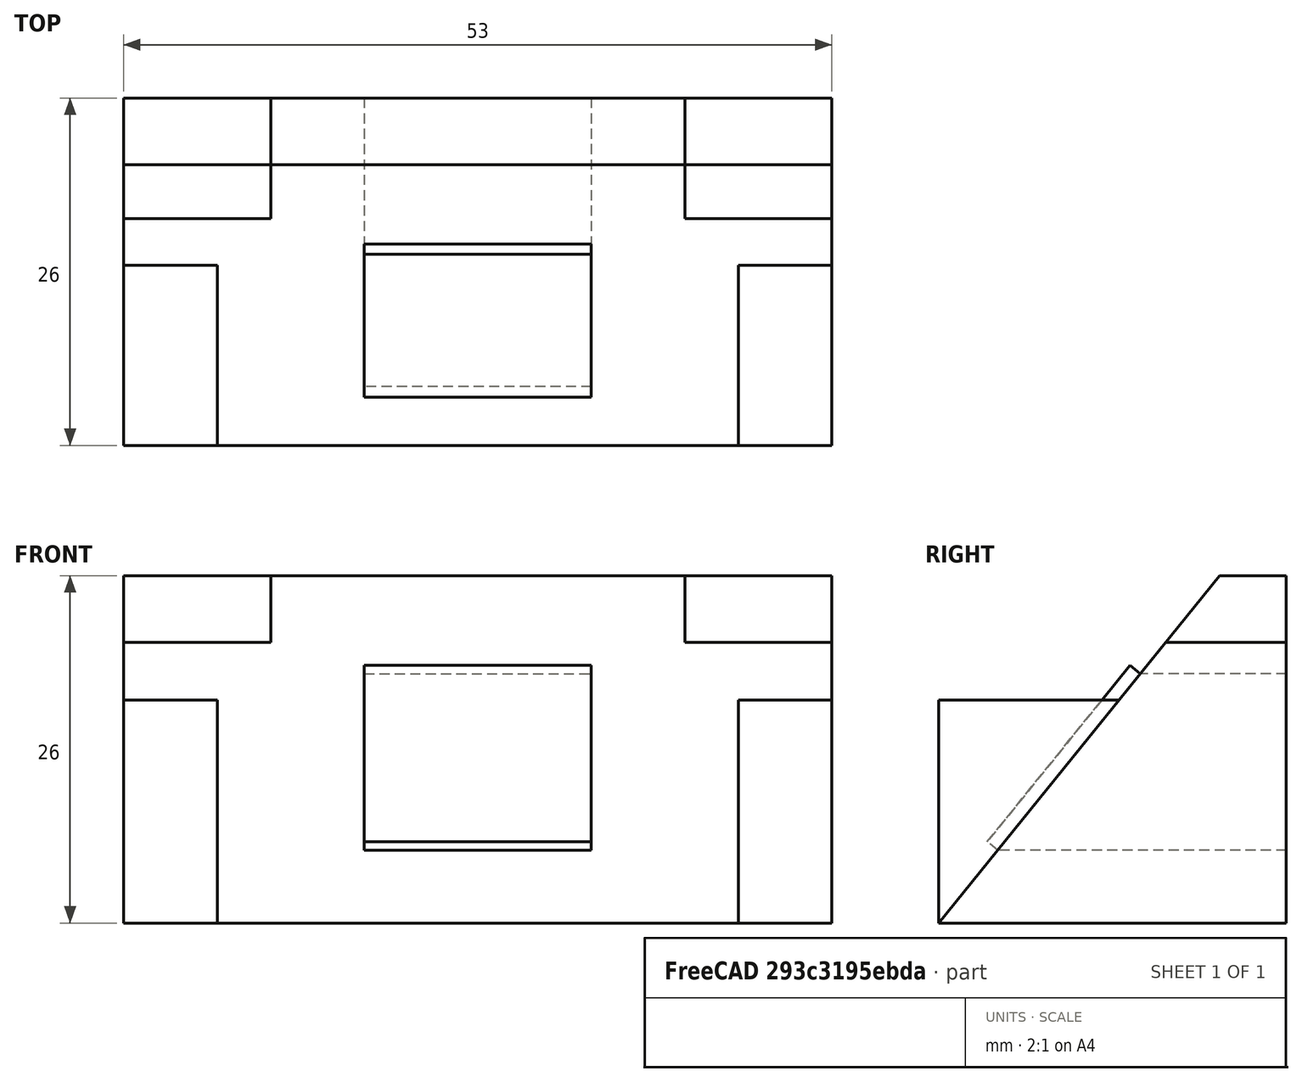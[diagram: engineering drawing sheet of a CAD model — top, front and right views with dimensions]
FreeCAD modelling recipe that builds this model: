
FCSTD DOCUMENT  (FreeCAD 0.16R)
Label: tutorial1
License: All rights reserved
LicenseURL: http://en.wikipedia.org/wiki/All_rights_reserved
objects: Sketcher::SketchObject×5, PartDesign::Pad×3, PartDesign::Pocket×2, PartDesign::Mirrored×2, Mesh::Feature×2, Part::FeaturePython×1
note: 18 computed .brp shape members not serialized (recipe doc carries the construction recipe); baked Part::Feature solids carry a one-line shape summary decoded from their .brp

FEATURE [Sketcher::SketchObject] Sketch
  Placement = pos=(0,0,0) rot=(0.57735,0.57735,0.57735;2.0944rad)
  sketch-geometry (4):
    g0: LineSegment StartX=8 StartY=13 StartZ=0 EndX=13 EndY=13 EndZ=0
    g1: LineSegment StartX=13 StartY=13 StartZ=0 EndX=13 EndY=-13 EndZ=0
    g2: LineSegment StartX=13 StartY=-13 StartZ=0 EndX=-13 EndY=-13 EndZ=0
    g3: LineSegment StartX=-13 StartY=-13 StartZ=0 EndX=8 EndY=13 EndZ=0
  constraints (11):
    c: Coincident(g0,g1)
    c: Vertical(g1)
    c: Coincident(g1,g2)
    c: Horizontal(g2)
    c: Coincident(g2,g3)
    c: Horizontal(g0)
    c: Coincident(g3,g0)
    c: DistanceX(g2,g2) = 26
    c: DistanceX(g0,g0) = 5
    c: Equal(g2,g1)
    c: Symmetric(g2,g0,g-1)
FEATURE [PartDesign::Pad] Pad
  Length = 53
  Length2 = 1
  Midplane = true
  Placement = pos=(0,0,0) rot=(0.57735,0.57735,0.57735;2.0944rad)
  Sketch = -> Sketch
  Type = 0
FEATURE [Sketcher::SketchObject] Sketch001
  ExternalGeometry = -> [Pad]
  Placement = pos=(0,13,0) rot=(0.57735,0.57735,0.57735;4.18879rad)
  Support = -> Pad [Face2]
  sketch-geometry (4):
    g0: LineSegment StartX=8 StartY=26.5 StartZ=0 EndX=13 EndY=26.5 EndZ=0
    g1: LineSegment StartX=13 StartY=26.5 StartZ=0 EndX=13 EndY=15.5 EndZ=0
    g2: LineSegment StartX=13 StartY=15.5 StartZ=0 EndX=8 EndY=15.5 EndZ=0
    g3: LineSegment StartX=8 StartY=15.5 StartZ=0 EndX=8 EndY=26.5 EndZ=0
  constraints (11):
    c: Coincident(g0,g1)
    c: Coincident(g1,g2)
    c: Coincident(g2,g3)
    c: Coincident(g3,g0)
    c: Horizontal(g0)
    c: Horizontal(g2)
    c: Vertical(g1)
    c: Vertical(g3)
    c: DistanceX(g0,g0) = 5
    c: DistanceY(g1,g1) = 11
    c: Coincident(g-4,g0)
FEATURE [PartDesign::Pocket] Pocket
  Length = 5
  Placement = pos=(0,0,0) rot=(0.57735,0.57735,0.57735;2.0944rad)
  Sketch = -> Sketch001
  Type = 1
FEATURE [PartDesign::Mirrored] Mirrored
  MirrorPlane = -> Sketch001 [H_Axis]
  Originals = -> [Pocket]
  Placement = pos=(0,0,0) rot=(0.57735,0.57735,0.57735;2.0944rad)
FEATURE [Sketcher::SketchObject] Sketch002
  ExternalGeometry = -> [Mirrored]
  Placement = pos=(0,13,0) rot=(0.57735,0.57735,0.57735;4.18879rad)
  Support = -> Mirrored [Face2]
  sketch-geometry (4):
    g0: LineSegment StartX=-13 StartY=26.5 StartZ=0 EndX=3.7 EndY=26.5 EndZ=0
    g1: LineSegment StartX=3.7 StartY=26.5 StartZ=0 EndX=3.7 EndY=19.5 EndZ=0
    g2: LineSegment StartX=3.7 StartY=19.5 StartZ=0 EndX=-13 EndY=19.5 EndZ=0
    g3: LineSegment StartX=-13 StartY=19.5 StartZ=0 EndX=-13 EndY=26.5 EndZ=0
  constraints (11):
    c: Coincident(g0,g1)
    c: Coincident(g1,g2)
    c: Coincident(g2,g3)
    c: Coincident(g3,g0)
    c: Horizontal(g0)
    c: Horizontal(g2)
    c: Vertical(g1)
    c: Vertical(g3)
    c: DistanceX(g0,g0) = 16.7
    c: DistanceY(g1,g1) = 7
    c: Coincident(g0,g-3)
FEATURE [PartDesign::Pad] Pad001
  Length = 26
  Length2 = 100
  Placement = pos=(0,0,0) rot=(0.57735,0.57735,0.57735;2.0944rad)
  Reversed = true
  Sketch = -> Sketch002
  Type = 0
FEATURE [PartDesign::Mirrored] Mirrored001
  MirrorPlane = -> Sketch002 [H_Axis]
  Originals = -> [Pad001]
  Placement = pos=(0,0,0) rot=(0.57735,0.57735,0.57735;2.0944rad)
FEATURE [Sketcher::SketchObject] Sketch003
  ExternalGeometry = -> [Mirrored001]
  Placement = pos=(0,-1.51298,1.22202) rot=(0.395866,0.395866,-0.828601;1.75771rad)
  Support = -> Mirrored001 [Face4]
  sketch-geometry (4):
    g0: LineSegment StartX=-5.71838 StartY=8.5 StartZ=0 EndX=11.2816 EndY=8.5 EndZ=0
    g1: LineSegment StartX=11.2816 StartY=8.5 StartZ=0 EndX=11.2816 EndY=-8.5 EndZ=0
    g2: LineSegment StartX=11.2816 StartY=-8.5 StartZ=0 EndX=-5.71838 EndY=-8.5 EndZ=0
    g3: LineSegment StartX=-5.71838 StartY=-8.5 StartZ=0 EndX=-5.71838 EndY=8.5 EndZ=0
  constraints (12):
    c: Coincident(g0,g1)
    c: Coincident(g1,g2)
    c: Coincident(g2,g3)
    c: Coincident(g3,g0)
    c: Horizontal(g0)
    c: Horizontal(g2)
    c: Vertical(g1)
    c: Vertical(g3)
    c: DistanceX(g0,g0) = 17
    c: DistanceY(g1,g1) = 17
    c: DistanceX(g0,g-4) = 7
    c: DistanceY(g0,g-4) = 11
FEATURE [PartDesign::Pad] Pad002
  Length = 1
  Length2 = 100
  Placement = pos=(0,0,0) rot=(0.57735,0.57735,0.57735;2.0944rad)
  Sketch = -> Sketch003
  Type = 0
FEATURE [Sketcher::SketchObject] Sketch004
  ExternalGeometry = -> [Pad002]
  Placement = pos=(0,13,0) rot=(0.57735,0.57735,0.57735;4.18879rad)
  Support = -> Pad002 [Face2]
  sketch-geometry (4):
    g0: LineSegment StartX=5.67059 StartY=8.5 StartZ=0 EndX=-7.55441 EndY=8.5 EndZ=0
    g1: LineSegment StartX=-7.55441 StartY=8.5 StartZ=0 EndX=-7.55441 EndY=-8.5 EndZ=0
    g2: LineSegment StartX=-7.55441 StartY=-8.5 StartZ=0 EndX=5.67059 EndY=-8.5 EndZ=0
    g3: LineSegment StartX=5.67059 StartY=-8.5 StartZ=0 EndX=5.67059 EndY=8.5 EndZ=0
  constraints (10):
    c: Coincident(g0,g1)
    c: Coincident(g1,g2)
    c: Coincident(g2,g3)
    c: Coincident(g3,g0)
    c: Horizontal(g0)
    c: Horizontal(g2)
    c: Vertical(g1)
    c: Vertical(g3)
    c: Coincident(g0,g-5)
    c: Coincident(g-4,g1)
FEATURE [PartDesign::Pocket] Pocket001
  Length = 5
  Placement = pos=(0,0,0) rot=(0.57735,0.57735,0.57735;2.0944rad)
  Sketch = -> Sketch004
  Type = 1
FEATURE [Part::FeaturePython] refine  label="refine_Pocket001"  # WARN: FeaturePython — macro-defined, semantics opaque (R4)
  Base = -> Pocket001
FEATURE [Mesh::Feature] Mesh  label="refine_Pocket001 (Meshed)"
FEATURE [Mesh::Feature] Mesh001  label="refine_Pocket001 (Meshed)001"
